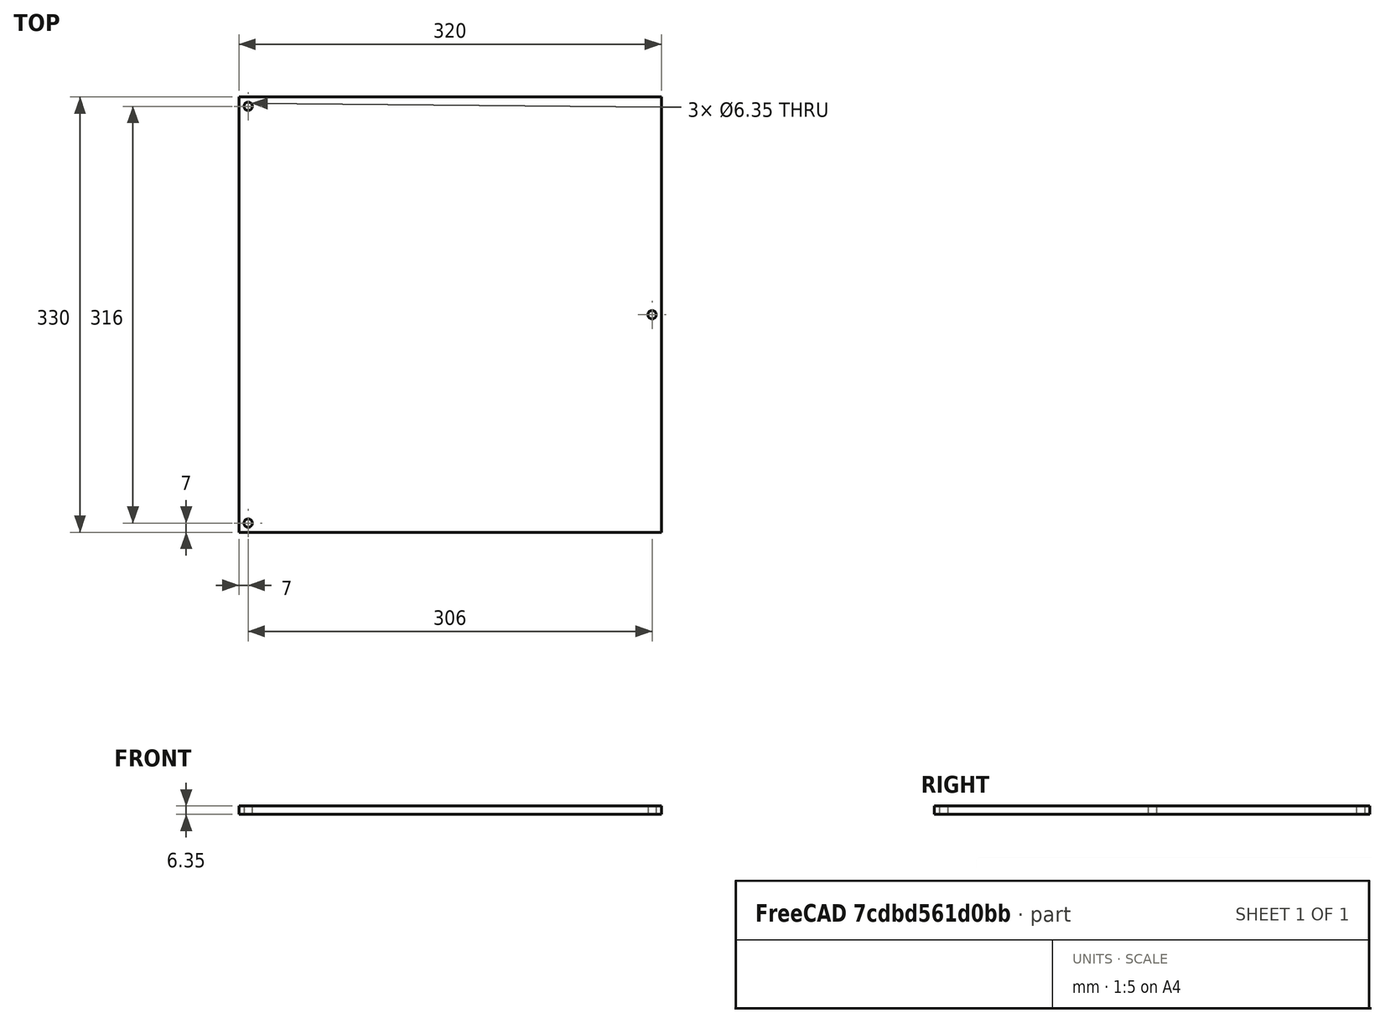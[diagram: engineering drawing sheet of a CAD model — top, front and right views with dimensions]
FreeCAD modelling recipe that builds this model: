
FCSTD DOCUMENT  (FreeCAD 0.19R23578 (Git))
Label: bed_plate
License: All rights reserved
LicenseURL: http://en.wikipedia.org/wiki/All_rights_reserved
objects: Sketcher::SketchObject×1, PartDesign::Pad×1, PartDesign::Body×1
note: 4 computed .brp shape members not serialized (recipe doc carries the construction recipe); baked Part::Feature solids carry a one-line shape summary decoded from their .brp

FEATURE [Sketcher::SketchObject] Sketch013
  MapMode = 5
  Support = -> [XY_Plane016]
  sketch-geometry (7):
    g0: LineSegment StartX=-160 StartY=165 StartZ=0 EndX=160 EndY=165 EndZ=0
    g1: LineSegment StartX=160 StartY=165 StartZ=0 EndX=160 EndY=-165 EndZ=0
    g2: LineSegment StartX=160 StartY=-165 StartZ=0 EndX=-160 EndY=-165 EndZ=0
    g3: LineSegment StartX=-160 StartY=-165 StartZ=0 EndX=-160 EndY=165 EndZ=0
    g4: Circle CenterX=-153 CenterY=158 CenterZ=0 NormalX=0 NormalY=0 NormalZ=1 AngleXU=0 Radius=3.175
    g5: Circle CenterX=-153 CenterY=-158 CenterZ=0 NormalX=0 NormalY=0 NormalZ=1 AngleXU=0 Radius=3.175
    g6: Circle CenterX=153 CenterY=0 CenterZ=0 NormalX=0 NormalY=0 NormalZ=1 AngleXU=0 Radius=3.175
  constraints (20):
    c: Coincident(g0,g1)
    c: Coincident(g1,g2)
    c: Coincident(g2,g3)
    c: Coincident(g3,g0)
    c: Horizontal(g0)
    c: Horizontal(g2)
    c: Vertical(g1)
    c: Vertical(g3)
    c: DistanceX(g0,g0) = 320  'bed_w'
    c: DistanceY(g1,g1) = 330  'bed_d'
    c: DistanceY(g-1,g0) = 165
    c: DistanceX(g-1,g0) = 160
    c: DistanceX(g4,g-1) = 153
    c: DistanceY(g-1,g4) = 158
    c: Symmetric(g4,g5,g-1)
    c: PointOnObject(g6,g-1)
    c: DistanceX(g-1,g6) = 153
    c: Equal(g4,g5)
    c: Equal(g5,g6)
    c: Diameter(g4) = 6.35  'adj_screw_dia'
FEATURE [PartDesign::Pad] Pad006
  AllowMultiFace = false
  Direction = (1,1,1)
  Length = 6.35
  Length2 = 100
  Profile = -> Sketch013
  Type = 0
FEATURE [PartDesign::Body] Body006  label="bed_plate"
  Group = -> [Sketch013,Pad006]
  Origin = -> Origin016
  Tip = -> Pad006
